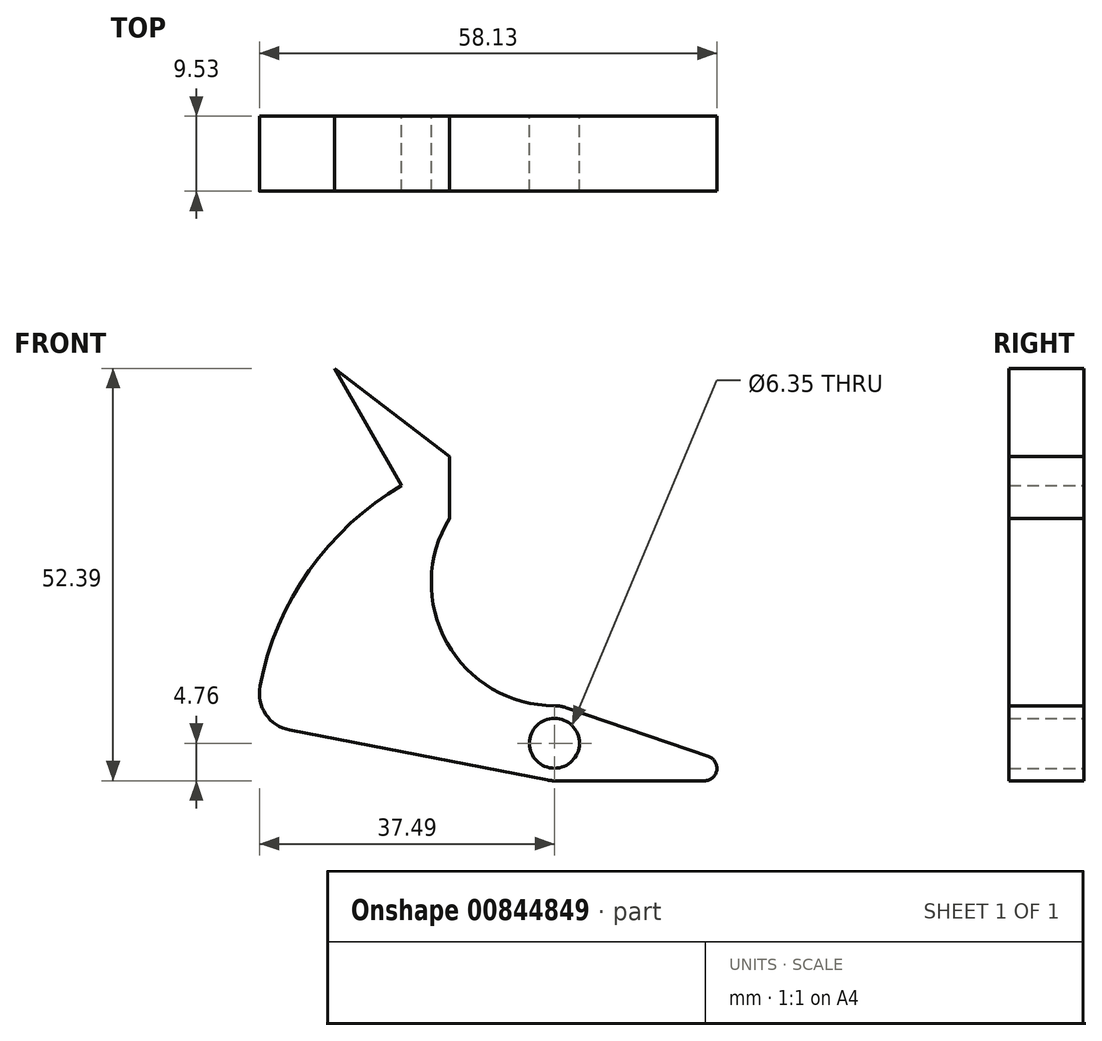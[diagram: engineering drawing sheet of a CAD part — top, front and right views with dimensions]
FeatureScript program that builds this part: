
annotation { "Feature Type Name" : "Feature", "Feature Type Description" : "" }
export const myFeature = defineFeature(function(context is Context, id is Id, definition is map)
    precondition{}
    {
        {
            var Q0;
            Q0=qCreatedBy(makeId("Front.planeOp"),FACE);
            var sketch = newSketch(context, id + "F0", { "sketchPlane" : qUnion([Q0])});
            skCircle(sketch, "E0", {"center": v(0, 0) * mm, "radius": 38.1 * mm});
            skCircle(sketch, "E1", {"center": v(0, 0) * mm, "radius": 4.76 * mm});
            skCircle(sketch, "E2", {"center": v(0, 0) * mm, "radius": 3.18 * mm});
            skLineSegment(sketch, "E3", {"start": v(-34.27, 1.8) * mm, "end": v(-0.9, -4.68) * mm});
            skLineSegment(sketch, "E4", {"start": v(-13.34, 28.58) * mm, "end": v(-13.34, 36.4) * mm});
            skLineSegment(sketch, "E5", {"start": v(-13.34, 36.4) * mm, "end": v(-27.94, 47.63) * mm});
            skLineSegment(sketch, "E6", {"start": v(-27.94, 47.63) * mm, "end": v(-19.43, 32.78) * mm});
            skCircle(sketch, "E7", {"center": v(0, 20.4) * mm, "radius": 15.64 * mm});
            skLineSegment(sketch, "E8", {"start": v(0, 0) * mm, "end": v(-54.7, 10.61) * mm});
            skCircle(sketch, "E9", {"center": v(-32.73, 6.35) * mm, "radius": 4.76 * mm});
            skLineSegment(sketch, "E10", {"start": v(47.35, -4.76) * mm, "end": v(-19.8, -4.76) * mm});
            skCircle(sketch, "E11", {"center": v(19.05, -3.17) * mm, "radius": 1.59 * mm});
            skLineSegment(sketch, "E12", {"start": v(26.01, -3.88) * mm, "end": v(-23.42, 13.07) * mm});
            skSolve(sketch);
        }
        {
            var Q0;
            {var subQ4=sQuery(id+"F0.wireOp",EDGE,"E5");Q0=makeQuery(id+"F0.imprint","IMPRINT",FACE,{"disambiguationData":[TD([[makeQuery(id+"F0.imprint","IMPRINT",EDGE,{"derivedFrom":subQ4}),1.0]])]});}
            var Q1;
            {var subQ0=sQuery(id+"F0.wireOp",EDGE,"E9");var subQ1=sQuery(id+"F0.wireOp",EDGE,"E8");var subQ3=makeQuery(id+"F0.imprint","INTERSECT",VERTEX,{"derivedFrom":[subQ1,subQ0]});Q1=makeQuery(id+"F0.imprint","IMPRINT",FACE,{"disambiguationData":[TD([[makeQuery(id+"F0.imprint","IMPRINT",EDGE,{"disambiguationData":[TD([[subQ3,-1.0]])],"derivedFrom":subQ1}),-1.0]])]});}
            var Q2;
            {var subQ0=sQuery(id+"F0.wireOp",EDGE,"E9");var subQ4=makeQuery(id+"F0.imprint","INTERSECT",VERTEX,{"derivedFrom":[sQuery(id+"F0.wireOp",EDGE,"E3"),subQ0]});Q2=makeQuery(id+"F0.imprint","IMPRINT",FACE,{"disambiguationData":[TD([[makeQuery(id+"F0.imprint","IMPRINT",EDGE,{"disambiguationData":[TD([[subQ4,-1.0]])],"derivedFrom":subQ0}),1.0]])]});}
            var Q3;
            {var subQ3=sQuery(id+"F0.wireOp",EDGE,"E0");var subQ5=makeQuery(id+"F0.imprint","INTERSECT",VERTEX,{"derivedFrom":[subQ3,sQuery(id+"F0.wireOp",EDGE,"E6")]});Q3=makeQuery(id+"F0.imprint","IMPRINT",FACE,{"disambiguationData":[TD([[makeQuery(id+"F0.imprint","IMPRINT",EDGE,{"disambiguationData":[TD([[subQ5,1.0]])],"derivedFrom":subQ3}),1.0]])]});}
            var Q4;
            {var subQ0=sQuery(id+"F0.wireOp",EDGE,"E3");var subQ1=sQuery(id+"F0.wireOp",EDGE,"E1");var subQ2=makeQuery(id+"F0.imprint","INTERSECT",VERTEX,{"derivedFrom":[subQ1,subQ0]});Q4=makeQuery(id+"F0.imprint","IMPRINT",FACE,{"disambiguationData":[TD([[makeQuery(id+"F0.imprint","IMPRINT",EDGE,{"disambiguationData":[TD([[subQ2,1.0]])],"derivedFrom":subQ1}),-1.0]])]});}
            var Q5;
            Q5=makeQuery(id+"F0.imprint","IMPRINT",FACE,{"disambiguationData":[TD([[makeQuery(id+"F0.imprint","IMPRINT",EDGE,{"derivedFrom":sQuery(id+"F0.wireOp",EDGE,"E2")}),-1.0]])]});
            var Q6;
            {var subQ0=sQuery(id+"F0.wireOp",EDGE,"E10");var subQ1=sQuery(id+"F0.wireOp",EDGE,"E1");var subQ2=makeQuery(id+"F0.imprint","INTERSECT",VERTEX,{"derivedFrom":[subQ1,subQ0]});Q6=makeQuery(id+"F0.imprint","IMPRINT",FACE,{"disambiguationData":[TD([[makeQuery(id+"F0.imprint","IMPRINT",EDGE,{"disambiguationData":[TD([[subQ2,-1.0]])],"derivedFrom":subQ1}),-1.0]])]});}
            var Q7;
            {var subQ0=sQuery(id+"F0.wireOp",EDGE,"E11");var subQ1=makeQuery(id+"F0.imprint","INTERSECT",VERTEX,{"derivedFrom":[subQ0,sQuery(id+"F0.wireOp",EDGE,"E12")]});Q7=makeQuery(id+"F0.imprint","IMPRINT",FACE,{"disambiguationData":[TD([[makeQuery(id+"F0.imprint","IMPRINT",EDGE,{"disambiguationData":[TD([[subQ1,-1.0]])],"derivedFrom":subQ0}),1.0]])]});}
            extrude(context, id + "F1", {"entities" : qUnion([Q0, Q1, Q2, Q3, Q4, Q5, Q6, Q7]), "depth" : 9.52 * mm, "offsetDistance" : 25.4 * mm});
        }
    });
